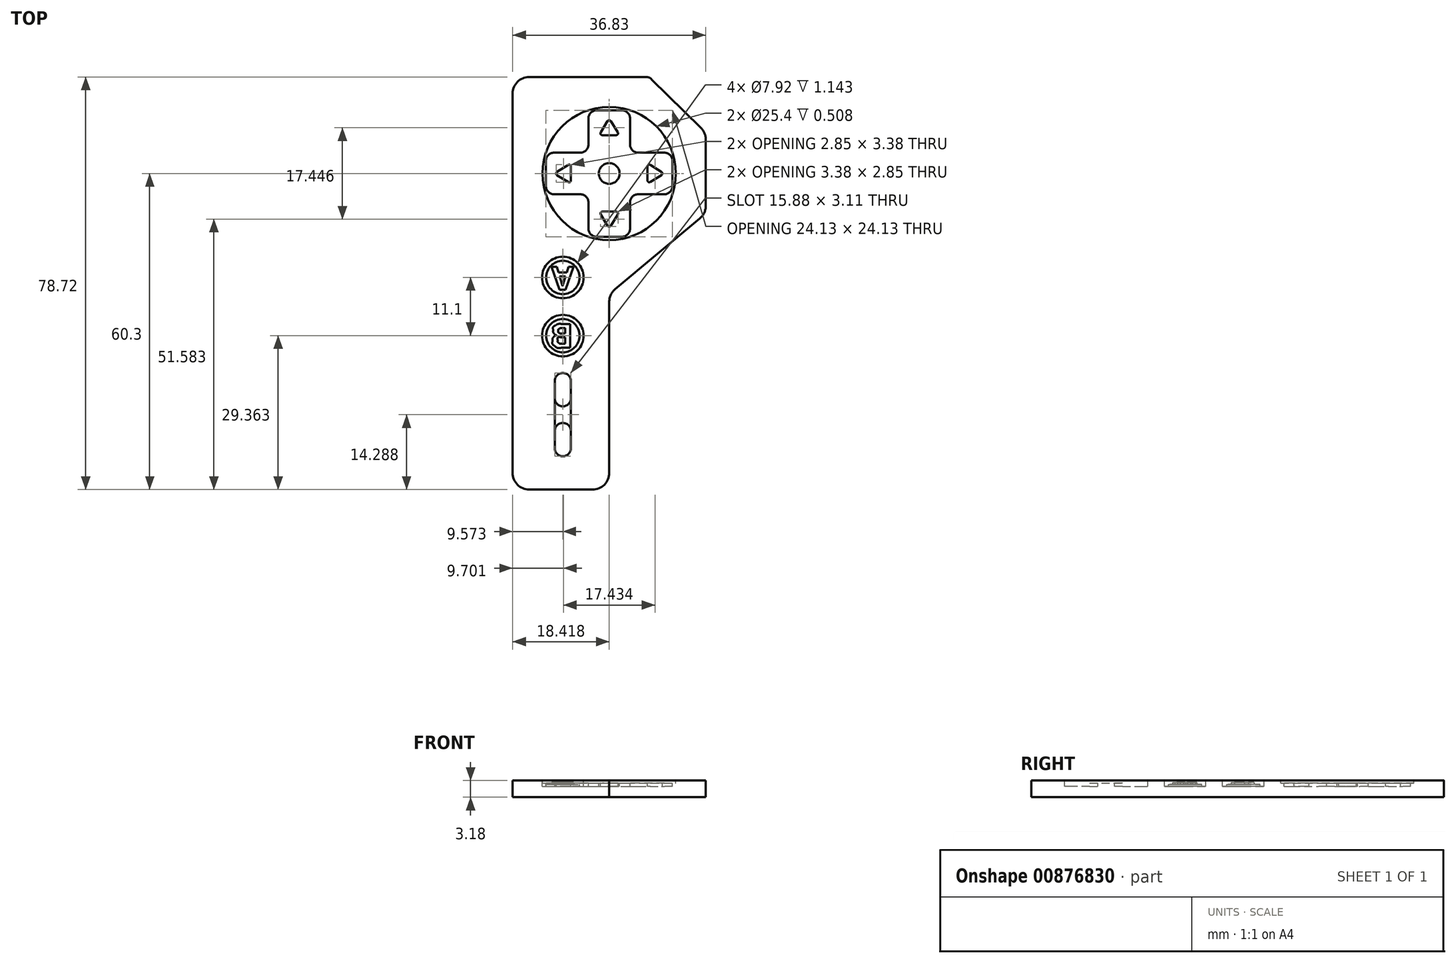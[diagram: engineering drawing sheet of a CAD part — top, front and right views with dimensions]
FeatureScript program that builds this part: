
annotation { "Feature Type Name" : "Feature", "Feature Type Description" : "" }
export const myFeature = defineFeature(function(context is Context, id is Id, definition is map)
    precondition{}
    {
        {
            var Q0;
            Q0=qCreatedBy(makeId("Top.planeOp"),FACE);
            var sketch = newSketch(context, id + "F0", { "sketchPlane" : qUnion([Q0])});
            skCircle(sketch, "E0", {"center": v(0, 0) * mm, "radius": 12.7 * mm});
            skLineSegment(sketch, "E1", {"start": v(3.96, 5.52) * mm, "end": v(3.96, 10.51) * mm});
            skLineSegment(sketch, "E2", {"start": v(2.4, 12.07) * mm, "end": v(0, 12.07) * mm});
            skLineSegment(sketch, "E3", {"start": v(0, 12.07) * mm, "end": v(-2.4, 12.07) * mm});
            skLineSegment(sketch, "E4", {"start": v(-3.96, 5.52) * mm, "end": v(-3.96, 10.51) * mm});
            skLineSegment(sketch, "E5", {"start": v(-3.96, -5.52) * mm, "end": v(-3.96, -10.51) * mm});
            skLineSegment(sketch, "E6", {"start": v(-2.4, -12.07) * mm, "end": v(2.4, -12.07) * mm});
            skLineSegment(sketch, "E7", {"start": v(3.96, -10.51) * mm, "end": v(3.96, -5.52) * mm});
            skLineSegment(sketch, "E8", {"start": v(5.52, 3.96) * mm, "end": v(10.51, 3.96) * mm});
            skLineSegment(sketch, "E9", {"start": v(12.07, 2.4) * mm, "end": v(12.07, -2.4) * mm});
            skLineSegment(sketch, "E10", {"start": v(10.51, -3.96) * mm, "end": v(5.52, -3.96) * mm});
            skLineSegment(sketch, "E11", {"start": v(-5.52, -3.96) * mm, "end": v(-10.51, -3.96) * mm});
            skLineSegment(sketch, "E12", {"start": v(-12.07, -2.4) * mm, "end": v(-12.07, 2.4) * mm});
            skLineSegment(sketch, "E13", {"start": v(-10.51, 3.96) * mm, "end": v(-5.52, 3.96) * mm});
            skLineSegment(sketch, "E14", {"start": v(-12.07, 0) * mm, "end": v(-12.07, 2.4) * mm});
            skLineSegment(sketch, "E15", {"start": v(12.07, 2.4) * mm, "end": v(12.07, 0) * mm});
            skLineSegment(sketch, "E16", {"start": v(12.07, 0) * mm, "end": v(12.07, -2.4) * mm});
            skLineSegment(sketch, "E17", {"start": v(-12.07, 0) * mm, "end": v(-12.07, -2.4) * mm});
            skLineSegment(sketch, "E18", {"start": v(0, 7.3) * mm, "end": v(-1.33, 7.3) * mm});
            skLineSegment(sketch, "E19", {"start": v(-1.63, 7.86) * mm, "end": v(-0.3, 9.98) * mm});
            skLineSegment(sketch, "E20", {"start": v(0, 7.3) * mm, "end": v(1.33, 7.3) * mm});
            skLineSegment(sketch, "E21", {"start": v(1.63, 7.86) * mm, "end": v(0.3, 9.98) * mm});
            skLineSegment(sketch, "E22", {"start": v(7.3, 0) * mm, "end": v(7.3, 1.33) * mm});
            skLineSegment(sketch, "E23", {"start": v(7.85, 1.63) * mm, "end": v(9.97, 0.3) * mm});
            skLineSegment(sketch, "E24", {"start": v(7.3, 0) * mm, "end": v(7.3, -1.33) * mm});
            skLineSegment(sketch, "E25", {"start": v(7.85, -1.63) * mm, "end": v(9.97, -0.3) * mm});
            skLineSegment(sketch, "E26", {"start": v(0, -7.3) * mm, "end": v(1.33, -7.3) * mm});
            skLineSegment(sketch, "E27", {"start": v(1.63, -7.85) * mm, "end": v(0.3, -9.97) * mm});
            skLineSegment(sketch, "E28", {"start": v(0, -7.3) * mm, "end": v(-1.33, -7.3) * mm});
            skLineSegment(sketch, "E29", {"start": v(-1.63, -7.85) * mm, "end": v(-0.3, -9.97) * mm});
            skLineSegment(sketch, "E30", {"start": v(-7.3, 0) * mm, "end": v(-7.3, 1.33) * mm});
            skLineSegment(sketch, "E31", {"start": v(-7.85, 1.63) * mm, "end": v(-9.97, 0.3) * mm});
            skLineSegment(sketch, "E32", {"start": v(-7.3, 0) * mm, "end": v(-7.3, -1.33) * mm});
            skLineSegment(sketch, "E33", {"start": v(-7.85, -1.63) * mm, "end": v(-9.97, -0.3) * mm});
            skCircle(sketch, "E34", {"center": v(0, 0) * mm, "radius": 1.98 * mm});
            skPoint(sketch, "E35.start.orphan", {"position": v(-1.98, 12.07) * mm});
            skPoint(sketch, "E36.start.orphan", {"position": v(1.98, 12.07) * mm});
            skPoint(sketch, "E37.orphan", {"position": v(-12.07, 1.98) * mm});
            skPoint(sketch, "E38.orphan", {"position": v(-12.07, -1.98) * mm});
            skPoint(sketch, "E39.end.orphan", {"position": v(12.07, 1.98) * mm});
            skPoint(sketch, "E40.trimOffspring.end.orphan", {"position": v(12.07, -1.98) * mm});
            skPoint(sketch, "E41.start.orphan", {"position": v(0, -12.07) * mm});
            skCircle(sketch, "E42", {"center": v(8.85, -19.84) * mm, "radius": 3.96 * mm});
            skCircle(sketch, "E43", {"center": v(8.85, -30.94) * mm, "radius": 3.96 * mm});
            skCircle(sketch, "E44", {"center": v(8.85, -19.84) * mm, "radius": 3.18 * mm});
            skCircle(sketch, "E45", {"center": v(8.85, -30.94) * mm, "radius": 3.18 * mm});
            skPoint(sketch, "E46.visualSharp", {"position": v(-3.96, 3.96) * mm});
            skArc(sketch, "E46.filletArc", {"start": v(-5.52, 3.96) * mm, "mid": v(-4.42, 4.42) * mm, "end": v(-3.96, 5.52) * mm});
            skPoint(sketch, "E47.visualSharp", {"position": v(3.96, 3.96) * mm});
            skArc(sketch, "E47.filletArc", {"start": v(3.96, 5.52) * mm, "mid": v(4.42, 4.42) * mm, "end": v(5.52, 3.96) * mm});
            skPoint(sketch, "E48.visualSharp", {"position": v(-3.96, 12.07) * mm});
            skArc(sketch, "E48.filletArc", {"start": v(-2.4, 12.07) * mm, "mid": v(-3.5, 11.61) * mm, "end": v(-3.96, 10.51) * mm});
            skPoint(sketch, "E49.visualSharp", {"position": v(3.96, 12.07) * mm});
            skArc(sketch, "E49.filletArc", {"start": v(3.96, 10.51) * mm, "mid": v(3.5, 11.61) * mm, "end": v(2.4, 12.07) * mm});
            skPoint(sketch, "E50.visualSharp", {"position": v(12.07, 3.96) * mm});
            skArc(sketch, "E50.filletArc", {"start": v(12.07, 2.4) * mm, "mid": v(11.61, 3.5) * mm, "end": v(10.51, 3.96) * mm});
            skPoint(sketch, "E51.visualSharp", {"position": v(12.07, -3.96) * mm});
            skArc(sketch, "E51.filletArc", {"start": v(10.51, -3.96) * mm, "mid": v(11.61, -3.5) * mm, "end": v(12.07, -2.4) * mm});
            skPoint(sketch, "E52.visualSharp", {"position": v(3.96, -3.96) * mm});
            skArc(sketch, "E52.filletArc", {"start": v(5.52, -3.96) * mm, "mid": v(4.42, -4.42) * mm, "end": v(3.96, -5.52) * mm});
            skPoint(sketch, "E53.visualSharp", {"position": v(3.96, -12.07) * mm});
            skArc(sketch, "E53.filletArc", {"start": v(2.4, -12.07) * mm, "mid": v(3.5, -11.61) * mm, "end": v(3.96, -10.51) * mm});
            skPoint(sketch, "E54.visualSharp", {"position": v(-3.96, -12.07) * mm});
            skArc(sketch, "E54.filletArc", {"start": v(-3.96, -10.51) * mm, "mid": v(-3.5, -11.61) * mm, "end": v(-2.4, -12.07) * mm});
            skPoint(sketch, "E55.visualSharp", {"position": v(-3.96, -3.96) * mm});
            skArc(sketch, "E55.filletArc", {"start": v(-3.96, -5.52) * mm, "mid": v(-4.42, -4.42) * mm, "end": v(-5.52, -3.96) * mm});
            skPoint(sketch, "E56.visualSharp", {"position": v(-12.07, -3.96) * mm});
            skArc(sketch, "E56.filletArc", {"start": v(-12.07, -2.4) * mm, "mid": v(-11.61, -3.5) * mm, "end": v(-10.51, -3.96) * mm});
            skPoint(sketch, "E57.visualSharp", {"position": v(-12.07, 3.96) * mm});
            skArc(sketch, "E57.filletArc", {"start": v(-10.51, 3.96) * mm, "mid": v(-11.61, 3.5) * mm, "end": v(-12.07, 2.4) * mm});
            skPoint(sketch, "E58.visualSharp", {"position": v(-7.3, 1.98) * mm});
            skArc(sketch, "E58.filletArc", {"start": v(-7.3, 1.33) * mm, "mid": v(-7.48, 1.64) * mm, "end": v(-7.85, 1.63) * mm});
            skPoint(sketch, "E59.visualSharp", {"position": v(-10.47, 0) * mm});
            skArc(sketch, "E59.filletArc", {"start": v(-9.97, 0.3) * mm, "mid": v(-10.14, 0) * mm, "end": v(-9.97, -0.3) * mm});
            skPoint(sketch, "E60.visualSharp", {"position": v(-7.3, -1.98) * mm});
            skArc(sketch, "E60.filletArc", {"start": v(-7.85, -1.63) * mm, "mid": v(-7.48, -1.64) * mm, "end": v(-7.3, -1.33) * mm});
            skPoint(sketch, "E61.visualSharp", {"position": v(0, 10.48) * mm});
            skArc(sketch, "E61.filletArc", {"start": v(0.3, 9.98) * mm, "mid": v(0, 10.16) * mm, "end": v(-0.3, 9.98) * mm});
            skPoint(sketch, "E62.visualSharp", {"position": v(1.98, 7.3) * mm});
            skArc(sketch, "E62.filletArc", {"start": v(1.33, 7.3) * mm, "mid": v(1.64, 7.5) * mm, "end": v(1.63, 7.86) * mm});
            skPoint(sketch, "E63.visualSharp", {"position": v(-1.98, 7.3) * mm});
            skArc(sketch, "E63.filletArc", {"start": v(-1.63, 7.86) * mm, "mid": v(-1.64, 7.5) * mm, "end": v(-1.33, 7.3) * mm});
            skPoint(sketch, "E64.visualSharp", {"position": v(7.3, 1.98) * mm});
            skArc(sketch, "E64.filletArc", {"start": v(7.85, 1.63) * mm, "mid": v(7.48, 1.64) * mm, "end": v(7.3, 1.33) * mm});
            skPoint(sketch, "E65.visualSharp", {"position": v(10.47, 0) * mm});
            skArc(sketch, "E65.filletArc", {"start": v(9.97, -0.3) * mm, "mid": v(10.14, 0) * mm, "end": v(9.97, 0.3) * mm});
            skPoint(sketch, "E66.visualSharp", {"position": v(7.3, -1.98) * mm});
            skArc(sketch, "E66.filletArc", {"start": v(7.3, -1.33) * mm, "mid": v(7.48, -1.64) * mm, "end": v(7.85, -1.63) * mm});
            skPoint(sketch, "E67.visualSharp", {"position": v(1.98, -7.3) * mm});
            skArc(sketch, "E67.filletArc", {"start": v(1.63, -7.85) * mm, "mid": v(1.64, -7.48) * mm, "end": v(1.33, -7.3) * mm});
            skPoint(sketch, "E68.visualSharp", {"position": v(0, -10.47) * mm});
            skArc(sketch, "E68.filletArc", {"start": v(-0.3, -9.97) * mm, "mid": v(0, -10.14) * mm, "end": v(0.3, -9.97) * mm});
            skPoint(sketch, "E69.visualSharp", {"position": v(-1.98, -7.3) * mm});
            skArc(sketch, "E69.filletArc", {"start": v(-1.33, -7.3) * mm, "mid": v(-1.64, -7.48) * mm, "end": v(-1.63, -7.85) * mm});
            skLineSegment(sketch, "E70", {"start": v(0, -38.07) * mm, "end": v(0, -38.07) * mm});
            skLineSegment(sketch, "E71", {"start": v(10.4, -39.63) * mm, "end": v(10.4, -52.4) * mm});
            skLineSegment(sketch, "E72", {"start": v(7.3, -52.4) * mm, "end": v(7.3, -39.63) * mm});
            skLineSegment(sketch, "E73", {"start": v(0, -44.42) * mm, "end": v(0, -44.42) * mm});
            skLineSegment(sketch, "E74", {"start": v(0, -47.6) * mm, "end": v(0, -47.6) * mm});
            skLineSegment(sketch, "E75", {"start": v(7.3, -49.15) * mm, "end": v(7.3, -52.4) * mm});
            skLineSegment(sketch, "E76", {"start": v(10.4, -52.4) * mm, "end": v(10.4, -49.15) * mm});
            skLineSegment(sketch, "E77", {"start": v(7.3, -39.63) * mm, "end": v(7.3, -42.87) * mm});
            skLineSegment(sketch, "E78", {"start": v(10.4, -39.63) * mm, "end": v(10.4, -42.87) * mm});
            skPoint(sketch, "E79.visualSharp", {"position": v(7.3, -38.07) * mm});
            skArc(sketch, "E79.filletArc", {"start": v(8.85, -38.07) * mm, "mid": v(7.75, -38.53) * mm, "end": v(7.3, -39.63) * mm});
            skPoint(sketch, "E80.visualSharp", {"position": v(10.4, -38.07) * mm});
            skArc(sketch, "E80.filletArc", {"start": v(10.4, -39.63) * mm, "mid": v(9.94, -38.53) * mm, "end": v(8.85, -38.07) * mm});
            skPoint(sketch, "E81.visualSharp", {"position": v(7.3, -44.42) * mm});
            skArc(sketch, "E81.filletArc", {"start": v(7.3, -42.87) * mm, "mid": v(7.75, -43.97) * mm, "end": v(8.85, -44.42) * mm});
            skPoint(sketch, "E82.visualSharp", {"position": v(10.4, -44.42) * mm});
            skArc(sketch, "E82.filletArc", {"start": v(8.85, -44.42) * mm, "mid": v(9.94, -43.97) * mm, "end": v(10.4, -42.87) * mm});
            skPoint(sketch, "E83.visualSharp", {"position": v(7.3, -47.6) * mm});
            skArc(sketch, "E83.filletArc", {"start": v(8.85, -47.6) * mm, "mid": v(7.75, -48.05) * mm, "end": v(7.3, -49.15) * mm});
            skPoint(sketch, "E84.visualSharp", {"position": v(10.4, -47.6) * mm});
            skArc(sketch, "E84.filletArc", {"start": v(10.4, -49.15) * mm, "mid": v(9.94, -48.05) * mm, "end": v(8.85, -47.6) * mm});
            skPoint(sketch, "E85.visualSharp", {"position": v(7.3, -53.95) * mm});
            skArc(sketch, "E85.filletArc", {"start": v(7.3, -52.4) * mm, "mid": v(7.75, -53.5) * mm, "end": v(8.85, -53.95) * mm});
            skPoint(sketch, "E86.visualSharp", {"position": v(10.4, -53.95) * mm});
            skArc(sketch, "E86.filletArc", {"start": v(8.85, -53.95) * mm, "mid": v(9.94, -53.5) * mm, "end": v(10.4, -52.4) * mm});
            skLineSegment(sketch, "E87", {"start": v(3.18, -60.3) * mm, "end": v(12.07, -60.3) * mm});
            skLineSegment(sketch, "E88", {"start": v(12.07, -60.3) * mm, "end": v(15.24, -60.3) * mm});
            skLineSegment(sketch, "E89", {"start": v(18.42, -57.12) * mm, "end": v(18.42, 15.24) * mm});
            skLineSegment(sketch, "E90", {"start": v(0, 18.42) * mm, "end": v(15.24, 18.42) * mm});
            skLineSegment(sketch, "E91", {"start": v(0, 18.42) * mm, "end": v(-6.98, 18.42) * mm});
            skLineSegment(sketch, "E92", {"start": v(-18.42, 6.47) * mm, "end": v(-18.42, -6.15) * mm});
            skPoint(sketch, "E93.visualSharp", {"position": v(-18.42, 18.42) * mm});
            skPoint(sketch, "E94.visualSharp", {"position": v(18.42, 18.42) * mm});
            skArc(sketch, "E94.filletArc", {"start": v(18.42, 15.24) * mm, "mid": v(17.49, 17.49) * mm, "end": v(15.24, 18.42) * mm});
            skPoint(sketch, "E95.visualSharp", {"position": v(18.42, -60.3) * mm});
            skArc(sketch, "E95.filletArc", {"start": v(15.24, -60.3) * mm, "mid": v(17.49, -59.37) * mm, "end": v(18.42, -57.12) * mm});
            skPoint(sketch, "E96.start.orphan", {"position": v(8.85, -12.7) * mm});
            skLineSegment(sketch, "E97", {"start": v(0, -50.77) * mm, "end": v(0, -24.5) * mm});
            skPoint(sketch, "E97.endSnap0", {"position": v(6.47, -19.84) * mm});
            skPoint(sketch, "E98.visualSharp", {"position": v(-18.42, -19.84) * mm});
            skPoint(sketch, "E99.visualSharp", {"position": v(0, -19.84) * mm});
            skLineSegment(sketch, "E100", {"start": v(-17.47, 8.73) * mm, "end": v(-8.07, 17.97) * mm});
            skLineSegment(sketch, "E101", {"start": v(-17.28, -8.59) * mm, "end": v(-1.14, -22.06) * mm});
            skPoint(sketch, "E102.orphan", {"position": v(-15.24, 18.42) * mm});
            skPoint(sketch, "E103.visualSharp", {"position": v(-7.62, 18.42) * mm});
            skArc(sketch, "E103.filletArc", {"start": v(-6.98, 18.42) * mm, "mid": v(-7.57, 18.3) * mm, "end": v(-8.07, 17.97) * mm});
            skPoint(sketch, "E104.visualSharp", {"position": v(-18.42, 7.8) * mm});
            skArc(sketch, "E104.filletArc", {"start": v(-17.47, 8.73) * mm, "mid": v(-18.17, 7.7) * mm, "end": v(-18.42, 6.47) * mm});
            skPoint(sketch, "E105.visualSharp", {"position": v(-18.42, -7.64) * mm});
            skArc(sketch, "E105.filletArc", {"start": v(-18.42, -6.15) * mm, "mid": v(-18.12, -7.5) * mm, "end": v(-17.28, -8.59) * mm});
            skPoint(sketch, "E106.visualSharp", {"position": v(0, -23.01) * mm});
            skArc(sketch, "E106.filletArc", {"start": v(0, -24.5) * mm, "mid": v(-0.3, -23.15) * mm, "end": v(-1.14, -22.06) * mm});
            skPoint(sketch, "E107.orphan", {"position": v(6.47, -23.01) * mm});
            skPoint(sketch, "E108.end.orphan", {"position": v(6.47, -16.66) * mm});
            skPoint(sketch, "E109.orphan", {"position": v(8.85, -15.87) * mm});
            skPoint(sketch, "E110.end.orphan", {"position": v(8.85, -23.8) * mm});
            skPoint(sketch, "E111.orphan", {"position": v(8.85, -26.97) * mm});
            skPoint(sketch, "E112.orphan", {"position": v(8.85, -34.9) * mm});
            skPoint(sketch, "E113.start.orphan", {"position": v(8.85, -53.95) * mm});
            skLineSegment(sketch, "E114", {"start": v(0, -50.77) * mm, "end": v(0, -57.12) * mm});
            skPoint(sketch, "E115.visualSharp", {"position": v(0, -60.3) * mm});
            skArc(sketch, "E115.filletArc", {"start": v(0, -57.12) * mm, "mid": v(0.93, -59.37) * mm, "end": v(3.18, -60.3) * mm});
            skSolve(sketch);
        }
        {
            var Q0;
            Q0=makeQuery(id+"F0.imprint","IMPRINT",FACE,{"disambiguationData":[TD([[makeQuery(id+"F0.imprint","IMPRINT",EDGE,{"derivedFrom":sQuery(id+"F0.wireOp",EDGE,"E0")}),-1.0]])]});
            var Q1;
            Q1=makeQuery(id+"F0.imprint","IMPRINT",FACE,{"disambiguationData":[TD([[makeQuery(id+"F0.imprint","IMPRINT",EDGE,{"derivedFrom":sQuery(id+"F0.wireOp",EDGE,"E0")}),1.0]])]});
            var Q2;
            Q2=makeQuery(id+"F0.imprint","IMPRINT",FACE,{"disambiguationData":[TD([[makeQuery(id+"F0.imprint","IMPRINT",EDGE,{"derivedFrom":sQuery(id+"F0.wireOp",EDGE,"E34")}),1.0]])]});
            var Q3;
            {var subQ1=sQuery(id+"F0.wireOp",EDGE,"PWhR1BMD-FvJ2-qZHG-oUCw-lLyY9EtCjW5L");Q3=makeQuery(id+"F0.imprint","IMPRINT",FACE,{"disambiguationData":[TD([[makeQuery(id+"F0.imprint","IMPRINT",EDGE,{"derivedFrom":subQ1}),-1.0]])]});}
            var Q4;
            Q4=makeQuery(id+"F0.imprint","IMPRINT",FACE,{"disambiguationData":[TD([[makeQuery(id+"F0.imprint","IMPRINT",EDGE,{"derivedFrom":sQuery(id+"F0.wireOp",EDGE,"E1")}),1.0]])]});
            var Q5;
            {var subQ0=sQuery(id+"F0.wireOp",EDGE,"E42");var subQ1=sQuery(id+"F0.wireOp",EDGE,"E110");var subQ2=makeQuery(id+"F0.imprint","INTERSECT",VERTEX,{"disambiguationData":[OD(1.0)],"derivedFrom":[subQ1,subQ0]});Q5=makeQuery(id+"F0.imprint","IMPRINT",FACE,{"disambiguationData":[TD([[makeQuery(id+"F0.imprint","IMPRINT",EDGE,{"disambiguationData":[TD([[subQ2,1.0]])],"derivedFrom":subQ1}),-1.0]])]});}
            var Q6;
            {var subQ0=sQuery(id+"F0.wireOp",EDGE,"E44");var subQ1=sQuery(id+"F0.wireOp",EDGE,"SsZxaRqU-6myA-YM92-NqyX-HjBMHzEltWH6");var subQ2=makeQuery(id+"F0.imprint","INTERSECT",VERTEX,{"disambiguationData":[OD(0.0)],"derivedFrom":[subQ1,subQ0]});Q6=makeQuery(id+"F0.imprint","IMPRINT",FACE,{"disambiguationData":[TD([[makeQuery(id+"F0.imprint","IMPRINT",EDGE,{"disambiguationData":[TD([[subQ2,-1.0]])],"derivedFrom":subQ1}),-1.0]])]});}
            var Q7;
            {var subQ0=sQuery(id+"F0.wireOp",EDGE,"E42");var subQ1=sQuery(id+"F0.wireOp",EDGE,"E110");var subQ2=makeQuery(id+"F0.imprint","INTERSECT",VERTEX,{"disambiguationData":[OD(1.0)],"derivedFrom":[subQ1,subQ0]});Q7=makeQuery(id+"F0.imprint","IMPRINT",FACE,{"disambiguationData":[TD([[makeQuery(id+"F0.imprint","IMPRINT",EDGE,{"disambiguationData":[TD([[subQ2,1.0]])],"derivedFrom":subQ1}),1.0]])]});}
            var Q8;
            {var subQ0=sQuery(id+"F0.wireOp",EDGE,"E44");var subQ1=sQuery(id+"F0.wireOp",EDGE,"E3AKRCSV-OPFl-1x9G-S51G-aRmQpPMT9qiU");var subQ2=makeQuery(id+"F0.imprint","INTERSECT",VERTEX,{"disambiguationData":[OD(0.0)],"derivedFrom":[subQ1,subQ0]});Q8=makeQuery(id+"F0.imprint","IMPRINT",FACE,{"disambiguationData":[TD([[makeQuery(id+"F0.imprint","IMPRINT",EDGE,{"disambiguationData":[TD([[subQ2,-1.0]])],"derivedFrom":subQ1}),-1.0]])]});}
            var Q9;
            {var subQ0=sQuery(id+"F0.wireOp",EDGE,"E45");var subQ1=sQuery(id+"F0.wireOp",EDGE,"zV0ygRvN-K9pG-sdqN-O0sk-nA2KY5Jrkro3");var subQ2=makeQuery(id+"F0.imprint","INTERSECT",VERTEX,{"disambiguationData":[OD(0.0)],"derivedFrom":[subQ1,subQ0]});Q9=makeQuery(id+"F0.imprint","IMPRINT",FACE,{"disambiguationData":[TD([[makeQuery(id+"F0.imprint","IMPRINT",EDGE,{"disambiguationData":[TD([[subQ2,-1.0]])],"derivedFrom":subQ1}),1.0]])]});}
            var Q10;
            {var subQ1=sQuery(id+"F0.wireOp",EDGE,"THAjXT8M-Z1Pn-Lz7r-dkB2-ijGnhJcu73TS");var subQ3=sQuery(id+"F0.wireOp",EDGE,"E45");var subQ4=makeQuery(id+"F0.imprint","INTERSECT",VERTEX,{"disambiguationData":[OD(1.0)],"derivedFrom":[subQ1,subQ3]});Q10=makeQuery(id+"F0.imprint","IMPRINT",FACE,{"disambiguationData":[TD([[makeQuery(id+"F0.imprint","IMPRINT",EDGE,{"disambiguationData":[TD([[subQ4,-1.0]])],"derivedFrom":subQ1}),-1.0]])]});}
            var Q11;
            {var subQ0=sQuery(id+"F0.wireOp",EDGE,"E45");var subQ1=sQuery(id+"F0.wireOp",EDGE,"THAjXT8M-Z1Pn-Lz7r-dkB2-ijGnhJcu73TS");var subQ2=makeQuery(id+"F0.imprint","INTERSECT",VERTEX,{"disambiguationData":[OD(0.0)],"derivedFrom":[subQ1,subQ0]});Q11=makeQuery(id+"F0.imprint","IMPRINT",FACE,{"disambiguationData":[TD([[makeQuery(id+"F0.imprint","IMPRINT",EDGE,{"disambiguationData":[TD([[subQ2,-1.0]])],"derivedFrom":subQ1}),1.0]])]});}
            var Q12;
            {var subQ1=sQuery(id+"F0.wireOp",EDGE,"UATAzTEx-YWs2-hctW-Svgk-vBC00LN1RAMS");Q12=makeQuery(id+"F0.imprint","IMPRINT",FACE,{"disambiguationData":[TD([[makeQuery(id+"F0.imprint","IMPRINT",EDGE,{"derivedFrom":subQ1}),-1.0]])]});}
            var Q13;
            {var subQ0=sQuery(id+"F0.wireOp",EDGE,"E43");var subQ1=sQuery(id+"F0.wireOp",EDGE,"rcpmd0S2-Yvhj-Z28p-Lw5I-cp6KCbKh0F2r");var subQ2=makeQuery(id+"F0.imprint","INTERSECT",VERTEX,{"disambiguationData":[OD(1.0)],"derivedFrom":[subQ1,subQ0]});Q13=makeQuery(id+"F0.imprint","IMPRINT",FACE,{"disambiguationData":[TD([[makeQuery(id+"F0.imprint","IMPRINT",EDGE,{"disambiguationData":[TD([[subQ2,1.0]])],"derivedFrom":subQ1}),1.0]])]});}
            var Q14;
            {var subQ0=sQuery(id+"F0.wireOp",EDGE,"E43");var subQ1=sQuery(id+"F0.wireOp",EDGE,"rcpmd0S2-Yvhj-Z28p-Lw5I-cp6KCbKh0F2r");var subQ2=makeQuery(id+"F0.imprint","INTERSECT",VERTEX,{"disambiguationData":[OD(1.0)],"derivedFrom":[subQ1,subQ0]});Q14=makeQuery(id+"F0.imprint","IMPRINT",FACE,{"disambiguationData":[TD([[makeQuery(id+"F0.imprint","IMPRINT",EDGE,{"disambiguationData":[TD([[subQ2,1.0]])],"derivedFrom":subQ1}),-1.0]])]});}
            var Q15;
            {var subQ0=sQuery(id+"F0.wireOp",EDGE,"UATAzTEx-YWs2-hctW-Svgk-vBC00LN1RAMS");Q15=makeQuery(id+"F0.imprint","IMPRINT",FACE,{"disambiguationData":[TD([[makeQuery(id+"F0.imprint","IMPRINT",EDGE,{"derivedFrom":subQ0}),1.0]])]});}
            var Q16;
            {var subQ0=sQuery(id+"F0.wireOp",EDGE,"MZkYzwrg-FkNa-l5V4-sU4M-MpxyEO5APBFG");Q16=makeQuery(id+"F0.imprint","IMPRINT",FACE,{"disambiguationData":[TD([[makeQuery(id+"F0.imprint","IMPRINT",EDGE,{"derivedFrom":subQ0}),1.0]])]});}
            var Q17;
            {var subQ0=sQuery(id+"F0.wireOp",EDGE,"SsZxaRqU-6myA-YM92-NqyX-HjBMHzEltWH6");var subQ3=sQuery(id+"F0.wireOp",EDGE,"E44");var subQ5=makeQuery(id+"F0.imprint","INTERSECT",VERTEX,{"disambiguationData":[OD(0.0)],"derivedFrom":[subQ0,subQ3]});Q17=makeQuery(id+"F0.imprint","IMPRINT",FACE,{"disambiguationData":[TD([[makeQuery(id+"F0.imprint","IMPRINT",EDGE,{"disambiguationData":[TD([[subQ5,1.0]])],"derivedFrom":subQ0}),1.0]])]});}
            var Q18;
            {var subQ1=sQuery(id+"F0.wireOp",EDGE,"PWhR1BMD-FvJ2-qZHG-oUCw-lLyY9EtCjW5L");Q18=makeQuery(id+"F0.imprint","IMPRINT",FACE,{"disambiguationData":[TD([[makeQuery(id+"F0.imprint","IMPRINT",EDGE,{"derivedFrom":subQ1}),1.0]])]});}
            var Q19;
            {var subQ0=sQuery(id+"F0.wireOp",EDGE,"3z70nU53-ivyG-1g0A-vYq8-NEXqmuddYAMu");Q19=makeQuery(id+"F0.imprint","IMPRINT",FACE,{"disambiguationData":[TD([[makeQuery(id+"F0.imprint","IMPRINT",EDGE,{"derivedFrom":subQ0}),-1.0]])]});}
            var Q20;
            {var subQ0=sQuery(id+"F0.wireOp",EDGE,"lPWCvXHn-auRQ-hYYK-SD1T-y9ubYwmYllBy");Q20=makeQuery(id+"F0.imprint","IMPRINT",FACE,{"disambiguationData":[TD([[makeQuery(id+"F0.imprint","IMPRINT",EDGE,{"derivedFrom":subQ0}),-1.0]])]});}
            var Q21;
            {var subQ1=sQuery(id+"F0.wireOp",EDGE,"E81.filletArc");Q21=makeQuery(id+"F0.imprint","IMPRINT",FACE,{"disambiguationData":[TD([[makeQuery(id+"F0.imprint","IMPRINT",EDGE,{"derivedFrom":subQ1}),-1.0]])]});}
            var Q22;
            {var subQ1=sQuery(id+"F0.wireOp",EDGE,"E3AKRCSV-OPFl-1x9G-S51G-aRmQpPMT9qiU");var subQ3=sQuery(id+"F0.wireOp",EDGE,"E44");var subQ4=makeQuery(id+"F0.imprint","INTERSECT",VERTEX,{"disambiguationData":[OD(1.0)],"derivedFrom":[subQ1,subQ3]});Q22=makeQuery(id+"F0.imprint","IMPRINT",FACE,{"disambiguationData":[TD([[makeQuery(id+"F0.imprint","IMPRINT",EDGE,{"disambiguationData":[TD([[subQ4,-1.0]])],"derivedFrom":subQ1}),1.0]])]});}
            var Q23;
            {var subQ3=sQuery(id+"F0.wireOp",EDGE,"MZkYzwrg-FkNa-l5V4-sU4M-MpxyEO5APBFG");Q23=makeQuery(id+"F0.imprint","IMPRINT",FACE,{"disambiguationData":[TD([[makeQuery(id+"F0.imprint","IMPRINT",EDGE,{"derivedFrom":subQ3}),-1.0]])]});}
            var Q24;
            {var subQ3=sQuery(id+"F0.wireOp",EDGE,"E108");Q24=makeQuery(id+"F0.imprint","IMPRINT",FACE,{"disambiguationData":[TD([[makeQuery(id+"F0.imprint","IMPRINT",EDGE,{"derivedFrom":subQ3}),-1.0]])]});}
            var Q25;
            {var subQ0=sQuery(id+"F0.wireOp",EDGE,"E108");Q25=makeQuery(id+"F0.imprint","IMPRINT",FACE,{"disambiguationData":[TD([[makeQuery(id+"F0.imprint","IMPRINT",EDGE,{"derivedFrom":subQ0}),1.0]])]});}
            var Q26;
            {var subQ0=sQuery(id+"F0.wireOp",EDGE,"zV0ygRvN-K9pG-sdqN-O0sk-nA2KY5Jrkro3");var subQ3=sQuery(id+"F0.wireOp",EDGE,"E45");var subQ5=makeQuery(id+"F0.imprint","INTERSECT",VERTEX,{"disambiguationData":[OD(0.0)],"derivedFrom":[subQ0,subQ3]});Q26=makeQuery(id+"F0.imprint","IMPRINT",FACE,{"disambiguationData":[TD([[makeQuery(id+"F0.imprint","IMPRINT",EDGE,{"disambiguationData":[TD([[subQ5,1.0]])],"derivedFrom":subQ0}),-1.0]])]});}
            var Q27;
            Q27=makeQuery(id+"F0.imprint","IMPRINT",FACE,{"disambiguationData":[TD([[makeQuery(id+"F0.imprint","IMPRINT",EDGE,{"derivedFrom":sQuery(id+"F0.wireOp",EDGE,"E22")}),-1.0]])]});
            var Q28;
            Q28=makeQuery(id+"F0.imprint","IMPRINT",FACE,{"disambiguationData":[TD([[makeQuery(id+"F0.imprint","IMPRINT",EDGE,{"derivedFrom":sQuery(id+"F0.wireOp",EDGE,"E113")}),-1.0]])]});
            var Q29;
            {var subQ3=sQuery(id+"F0.wireOp",EDGE,"3z70nU53-ivyG-1g0A-vYq8-NEXqmuddYAMu");Q29=makeQuery(id+"F0.imprint","IMPRINT",FACE,{"disambiguationData":[TD([[makeQuery(id+"F0.imprint","IMPRINT",EDGE,{"derivedFrom":subQ3}),1.0]])]});}
            var Q30;
            {var subQ3=sQuery(id+"F0.wireOp",EDGE,"lPWCvXHn-auRQ-hYYK-SD1T-y9ubYwmYllBy");Q30=makeQuery(id+"F0.imprint","IMPRINT",FACE,{"disambiguationData":[TD([[makeQuery(id+"F0.imprint","IMPRINT",EDGE,{"derivedFrom":subQ3}),1.0]])]});}
            var Q31;
            Q31=makeQuery(id+"F0.imprint","IMPRINT",FACE,{"disambiguationData":[TD([[makeQuery(id+"F0.imprint","IMPRINT",EDGE,{"derivedFrom":sQuery(id+"F0.wireOp",EDGE,"E113")}),1.0]])]});
            var Q32;
            Q32=makeQuery(id+"F0.imprint","IMPRINT",FACE,{"disambiguationData":[TD([[makeQuery(id+"F0.imprint","IMPRINT",EDGE,{"derivedFrom":sQuery(id+"F0.wireOp",EDGE,"KwRfv6RD-hlzn-2D6z-jxr3-LyIaI6EFIvGS")}),-1.0]])]});
            var Q33;
            Q33=makeQuery(id+"F0.imprint","IMPRINT",FACE,{"disambiguationData":[TD([[makeQuery(id+"F0.imprint","IMPRINT",EDGE,{"derivedFrom":sQuery(id+"F0.wireOp",EDGE,"KwRfv6RD-hlzn-2D6z-jxr3-LyIaI6EFIvGS")}),1.0]])]});
            var Q34;
            Q34=makeQuery(id+"F0.imprint","IMPRINT",FACE,{"disambiguationData":[TD([[makeQuery(id+"F0.imprint","IMPRINT",EDGE,{"derivedFrom":sQuery(id+"F0.wireOp",EDGE,"E18")}),-1.0]])]});
            var Q35;
            Q35=makeQuery(id+"F0.imprint","IMPRINT",FACE,{"disambiguationData":[TD([[makeQuery(id+"F0.imprint","IMPRINT",EDGE,{"derivedFrom":sQuery(id+"F0.wireOp",EDGE,"E30")}),1.0]])]});
            var Q36;
            Q36=makeQuery(id+"F0.imprint","IMPRINT",FACE,{"disambiguationData":[TD([[makeQuery(id+"F0.imprint","IMPRINT",EDGE,{"derivedFrom":sQuery(id+"F0.wireOp",EDGE,"E26")}),-1.0]])]});
            var Q37;
            Q37=makeQuery(id+"F0.imprint","IMPRINT",FACE,{"disambiguationData":[TD([[makeQuery(id+"F0.imprint","IMPRINT",EDGE,{"derivedFrom":sQuery(id+"F0.wireOp",EDGE,"E44")}),1.0]])]});
            var Q38;
            Q38=makeQuery(id+"F0.imprint","IMPRINT",FACE,{"disambiguationData":[TD([[makeQuery(id+"F0.imprint","IMPRINT",EDGE,{"derivedFrom":sQuery(id+"F0.wireOp",EDGE,"E45")}),1.0]])]});
            var Q39;
            Q39=makeQuery(id+"F0.imprint","IMPRINT",FACE,{"disambiguationData":[TD([[makeQuery(id+"F0.imprint","IMPRINT",EDGE,{"derivedFrom":sQuery(id+"F0.wireOp",EDGE,"E43")}),1.0]])]});
            var Q40;
            {var subQ1=sQuery(id+"F0.wireOp",EDGE,"E79.filletArc");Q40=makeQuery(id+"F0.imprint","IMPRINT",FACE,{"disambiguationData":[TD([[makeQuery(id+"F0.imprint","IMPRINT",EDGE,{"derivedFrom":subQ1}),1.0]])]});}
            var Q41;
            {var subQ1=sQuery(id+"F0.wireOp",EDGE,"E83.filletArc");Q41=makeQuery(id+"F0.imprint","IMPRINT",FACE,{"disambiguationData":[TD([[makeQuery(id+"F0.imprint","IMPRINT",EDGE,{"derivedFrom":subQ1}),1.0]])]});}
            var Q42;
            Q42=makeQuery(id+"F0.imprint","IMPRINT",FACE,{"disambiguationData":[TD([[makeQuery(id+"F0.imprint","IMPRINT",EDGE,{"derivedFrom":sQuery(id+"F0.wireOp",EDGE,"E42")}),1.0]])]});
            extrude(context, id + "F1", {"entities" : qUnion([Q0, Q1, Q2, Q3, Q4, Q5, Q6, Q7, Q8, Q9, Q10, Q11, Q12, Q13, Q14, Q15, Q16, Q17, Q18, Q19, Q20, Q21, Q22, Q23, Q24, Q25, Q26, Q27, Q28, Q29, Q30, Q31, Q32, Q33, Q34, Q35, Q36, Q37, Q38, Q39, Q40, Q41, Q42]), "depth" : 3.17 * mm, "offsetDistance" : 25.4 * mm});
        }
        {
            var Q0;
            Q0=makeQuery(id+"F0.imprint","IMPRINT",FACE,{"disambiguationData":[TD([[makeQuery(id+"F0.imprint","IMPRINT",EDGE,{"derivedFrom":sQuery(id+"F0.wireOp",EDGE,"E1")}),1.0]])]});
            extrude(context, id + "F2", {"entities" : qUnion([Q0]), "operationType" : NewBodyOperationType.REMOVE, "depth" : 1.14 * mm, "offsetDistance" : 25.4 * mm});
        }
        {
            var Q0;
            Q0=makeQuery(id+"F0.imprint","IMPRINT",FACE,{"disambiguationData":[TD([[makeQuery(id+"F0.imprint","IMPRINT",EDGE,{"derivedFrom":sQuery(id+"F0.wireOp",EDGE,"E0")}),1.0]])]});
            var Q1;
            Q1=makeQuery(id+"F0.imprint","IMPRINT",FACE,{"disambiguationData":[TD([[makeQuery(id+"F0.imprint","IMPRINT",EDGE,{"derivedFrom":sQuery(id+"F0.wireOp",EDGE,"E22")}),-1.0]])]});
            var Q2;
            Q2=makeQuery(id+"F0.imprint","IMPRINT",FACE,{"disambiguationData":[TD([[makeQuery(id+"F0.imprint","IMPRINT",EDGE,{"derivedFrom":sQuery(id+"F0.wireOp",EDGE,"E18")}),-1.0]])]});
            var Q3;
            Q3=makeQuery(id+"F0.imprint","IMPRINT",FACE,{"disambiguationData":[TD([[makeQuery(id+"F0.imprint","IMPRINT",EDGE,{"derivedFrom":sQuery(id+"F0.wireOp",EDGE,"E26")}),-1.0]])]});
            var Q4;
            Q4=makeQuery(id+"F0.imprint","IMPRINT",FACE,{"disambiguationData":[TD([[makeQuery(id+"F0.imprint","IMPRINT",EDGE,{"derivedFrom":sQuery(id+"F0.wireOp",EDGE,"E30")}),1.0]])]});
            var Q5;
            Q5=makeQuery(id+"F0.imprint","IMPRINT",FACE,{"disambiguationData":[TD([[makeQuery(id+"F0.imprint","IMPRINT",EDGE,{"derivedFrom":sQuery(id+"F0.wireOp",EDGE,"E34")}),1.0]])]});
            extrude(context, id + "F3", {"entities" : qUnion([Q0, Q1, Q2, Q3, Q4, Q5]), "operationType" : NewBodyOperationType.REMOVE, "depth" : 0.5 * mm, "offsetDistance" : 25.4 * mm});
        }
        {
            var Q0;
            Q0=makeQuery(id+"F0.imprint","IMPRINT",FACE,{"disambiguationData":[TD([[makeQuery(id+"F0.imprint","IMPRINT",EDGE,{"derivedFrom":sQuery(id+"F0.wireOp",EDGE,"E42")}),1.0]])]});
            var Q1;
            Q1=makeQuery(id+"F0.imprint","IMPRINT",FACE,{"disambiguationData":[TD([[makeQuery(id+"F0.imprint","IMPRINT",EDGE,{"derivedFrom":sQuery(id+"F0.wireOp",EDGE,"E43")}),1.0]])]});
            var Q2;
            {var subQ1=sQuery(id+"F0.wireOp",EDGE,"E79.filletArc");Q2=makeQuery(id+"F0.imprint","IMPRINT",FACE,{"disambiguationData":[TD([[makeQuery(id+"F0.imprint","IMPRINT",EDGE,{"derivedFrom":subQ1}),1.0]])]});}
            var Q3;
            {var subQ1=sQuery(id+"F0.wireOp",EDGE,"E83.filletArc");Q3=makeQuery(id+"F0.imprint","IMPRINT",FACE,{"disambiguationData":[TD([[makeQuery(id+"F0.imprint","IMPRINT",EDGE,{"derivedFrom":subQ1}),1.0]])]});}
            extrude(context, id + "F4", {"entities" : qUnion([Q0, Q1, Q2, Q3]), "operationType" : NewBodyOperationType.REMOVE, "depth" : 1.14 * mm, "offsetDistance" : 25.4 * mm});
        }
        {
            var Q0;
            Q0=makeQuery(id+"F0.imprint","IMPRINT",FACE,{"disambiguationData":[TD([[makeQuery(id+"F0.imprint","IMPRINT",EDGE,{"derivedFrom":sQuery(id+"F0.wireOp",EDGE,"E44")}),1.0]])]});
            var Q1;
            Q1=makeQuery(id+"F0.imprint","IMPRINT",FACE,{"disambiguationData":[TD([[makeQuery(id+"F0.imprint","IMPRINT",EDGE,{"derivedFrom":sQuery(id+"F0.wireOp",EDGE,"E45")}),1.0]])]});
            extrude(context, id + "F5", {"entities" : qUnion([Q0, Q1]), "operationType" : NewBodyOperationType.REMOVE, "depth" : 0.76 * mm, "offsetDistance" : 25.4 * mm});
        }
        {
            var Q0;
            Q0=makeQuery(id+"F5.boolean.opBoolean","COPY",FACE,{"derivedFrom":makeQuery(id+"F5.opExtrude","CAP_FACE",FACE,{"disambiguationData":[OSD([sQuery(id+"F0.wireOp",EDGE,"E44")])],"isStart":false})});
            var sketch = newSketch(context, id + "F6", { "sketchPlane" : qUnion([Q0])});
            skText(sketch, "E116", { "text": "A", "fontName": "OpenSans-Bold.ttf"});
            const initialGuessF6  = {"E116": [0.0068, 0.01782, 1, 0, 0.00438]};
            skSetInitialGuess(sketch, initialGuessF6);
            skSolve(sketch);
        }
        {
            var Q0;
            Q0=makeQuery(id+"F6.imprint","IMPRINT",FACE,{"disambiguationData":[TD([[makeQuery(id+"F6.imprint","IMPRINT",EDGE,{"derivedFrom":sQuery(id+"F6.wireOp",EDGE,"E116.sketch_text.stroke-0")}),-1.0]])]});
            extrude(context, id + "F7", {"entities" : qUnion([Q0]), "operationType" : NewBodyOperationType.ADD, "depth" : 0.38 * mm, "offsetDistance" : 25.4 * mm});
        }
        {
            var Q0;
            Q0=makeQuery(id+"F5.boolean.opBoolean","COPY",FACE,{"derivedFrom":makeQuery(id+"F5.opExtrude","CAP_FACE",FACE,{"disambiguationData":[OSD([sQuery(id+"F0.wireOp",EDGE,"E45")])],"isStart":false})});
            var sketch = newSketch(context, id + "F8", { "sketchPlane" : qUnion([Q0])});
            skLineSegment(sketch, "E117.0.0", {"start": v(7.45, 28.72) * mm, "end": v(7.45, 33.26) * mm});
            skLineSegment(sketch, "E117.0.1", {"start": v(7.45, 33.26) * mm, "end": v(9.14, 33.26) * mm});
            skFitSpline(sketch, "E117.0.2", {"points": [v(9.14, 33.26) * mm, v(9.91, 33.26) * mm, v(10.36, 32.91) * mm]});
            skFitSpline(sketch, "E117.0.3", {"points": [v(10.36, 32.91) * mm, v(10.81, 32.57) * mm, v(10.81, 31.94) * mm]});
            skFitSpline(sketch, "E117.0.4", {"points": [v(10.81, 31.94) * mm, v(10.81, 31.5) * mm, v(10.62, 31.24) * mm]});
            skFitSpline(sketch, "E117.0.5", {"points": [v(10.62, 31.24) * mm, v(10.43, 30.98) * mm, v(10, 30.88) * mm]});
            skLineSegment(sketch, "E117.0.6", {"start": v(10, 30.88) * mm, "end": v(10, 30.85) * mm});
            skFitSpline(sketch, "E117.0.7", {"points": [v(10, 30.85) * mm, v(10.32, 30.8) * mm, v(10.5, 30.54) * mm]});
            skFitSpline(sketch, "E117.0.8", {"points": [v(10.5, 30.54) * mm, v(10.7, 30.28) * mm, v(10.7, 29.87) * mm]});
            skFitSpline(sketch, "E117.0.9", {"points": [v(10.7, 29.87) * mm, v(10.7, 29.27) * mm, v(10.26, 29) * mm]});
            skFitSpline(sketch, "E117.0.10", {"points": [v(10.26, 29) * mm, v(9.83, 28.72) * mm, v(8.86, 28.72) * mm]});
            skLineSegment(sketch, "E117.0.11", {"start": v(8.86, 28.72) * mm, "end": v(7.45, 28.72) * mm});
            skLineSegment(sketch, "E118.0.0", {"start": v(8.92, 29.51) * mm, "end": v(8.41, 29.51) * mm});
            skLineSegment(sketch, "E118.0.1", {"start": v(8.41, 29.51) * mm, "end": v(8.41, 30.52) * mm});
            skLineSegment(sketch, "E118.0.2", {"start": v(8.41, 30.52) * mm, "end": v(8.97, 30.52) * mm});
            skFitSpline(sketch, "E118.0.3", {"points": [v(8.97, 30.52) * mm, v(9.36, 30.52) * mm, v(9.53, 30.4) * mm]});
            skFitSpline(sketch, "E118.0.4", {"points": [v(9.53, 30.4) * mm, v(9.7, 30.28) * mm, v(9.7, 30) * mm]});
            skFitSpline(sketch, "E118.0.5", {"points": [v(9.7, 30) * mm, v(9.7, 29.74) * mm, v(9.52, 29.62) * mm]});
            skFitSpline(sketch, "E118.0.6", {"points": [v(9.52, 29.62) * mm, v(9.33, 29.51) * mm, v(8.92, 29.51) * mm]});
            skFitSpline(sketch, "E118.1.0", {"points": [v(9.81, 31.85) * mm, v(9.81, 31.28) * mm, v(9, 31.28) * mm]});
            skLineSegment(sketch, "E118.1.1", {"start": v(9, 31.28) * mm, "end": v(8.41, 31.28) * mm});
            skLineSegment(sketch, "E118.1.2", {"start": v(8.41, 31.28) * mm, "end": v(8.41, 32.47) * mm});
            skLineSegment(sketch, "E118.1.3", {"start": v(8.41, 32.47) * mm, "end": v(9.04, 32.47) * mm});
            skFitSpline(sketch, "E118.1.4", {"points": [v(9.04, 32.47) * mm, v(9.43, 32.47) * mm, v(9.62, 32.31) * mm]});
            skFitSpline(sketch, "E118.1.5", {"points": [v(9.62, 32.31) * mm, v(9.81, 32.16) * mm, v(9.81, 31.85) * mm]});
            skSolve(sketch);
        }
        {
            var Q0;
            Q0=makeQuery(id+"F8.imprint","IMPRINT",FACE,{"disambiguationData":[TD([[makeQuery(id+"F8.imprint","IMPRINT",EDGE,{"derivedFrom":sQuery(id+"F8.wireOp",EDGE,"E117.0.0")}),-1.0]])]});
            extrude(context, id + "F9", {"entities" : qUnion([Q0]), "operationType" : NewBodyOperationType.ADD, "depth" : 0.38 * mm, "offsetDistance" : 25.4 * mm});
        }
        {
            var Q0;
            {var subQ1=sQuery(id+"F0.wireOp",EDGE,"E81.filletArc");Q0=makeQuery(id+"F0.imprint","IMPRINT",FACE,{"disambiguationData":[TD([[makeQuery(id+"F0.imprint","IMPRINT",EDGE,{"derivedFrom":subQ1}),-1.0]])]});}
            extrude(context, id + "F10", {"entities" : qUnion([Q0]), "operationType" : NewBodyOperationType.REMOVE, "depth" : 0.5 * mm, "offsetDistance" : 25.4 * mm});
        }
        {
            var Q0;
            Q0=makeQuery(id+"F1.opExtrude","CAP_EDGE",EDGE,{"disambiguationData":[OSD([sQuery(id+"F0.wireOp",EDGE,"E92")])],"isStart":false});
            cPoint(context, id + "F11", {"entities" : qUnion([Q0]), "parameter" : 0.5});
        }
        {
            var Q0;
            Q0=makeQuery(id+"F1.opExtrude","SWEPT_BODY",BODY,{"disambiguationData":[OSD([sQuery(id+"F0.wireOp",EDGE,"E87"),sQuery(id+"F0.wireOp",EDGE,"E88"),sQuery(id+"F0.wireOp",EDGE,"E89"),sQuery(id+"F0.wireOp",EDGE,"E90"),sQuery(id+"F0.wireOp",EDGE,"E91"),sQuery(id+"F0.wireOp",EDGE,"E92"),sQuery(id+"F0.wireOp",EDGE,"E94.filletArc"),sQuery(id+"F0.wireOp",EDGE,"E95.filletArc"),sQuery(id+"F0.wireOp",EDGE,"E97"),sQuery(id+"F0.wireOp",EDGE,"E100"),sQuery(id+"F0.wireOp",EDGE,"E101"),sQuery(id+"F0.wireOp",EDGE,"E103.filletArc"),sQuery(id+"F0.wireOp",EDGE,"E104.filletArc"),sQuery(id+"F0.wireOp",EDGE,"E105.filletArc"),sQuery(id+"F0.wireOp",EDGE,"E106.filletArc"),sQuery(id+"F0.wireOp",EDGE,"E114"),sQuery(id+"F0.wireOp",EDGE,"E115.filletArc")])]});
            var Q1;
            Q1 = qCreatedBy(id + "F11" ,VERTEX);
            var Q2;
            Q2=makeQuery(id+"F1.opExtrude","CAP_EDGE",EDGE,{"disambiguationData":[OSD([sQuery(id+"F0.wireOp",EDGE,"E92")])],"isStart":false});
            transform(context, id + "F12", {"entities" : qUnion([Q0]), "transformType" : TransformType.ROTATION, "transformAxis" : qUnion([Q2]), "angle" : 180 * degree, "makeCopy" : false});
        }
    });
